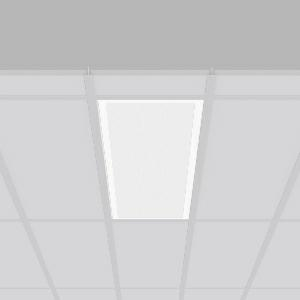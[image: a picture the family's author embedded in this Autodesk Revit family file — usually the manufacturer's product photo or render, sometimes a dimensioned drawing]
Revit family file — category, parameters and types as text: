
# Revit family: sidelite_eco_672375_002_1_1c27
name_source: partatom
category: Lighting Fixtures
units: mm (PartAtom-declared; Revit-internal decimal feet)

## family parameters
Cut with Voids When Loaded = No
Host = Face
Light Source = No
Part Type = Normal
Room Calculation Point = No
Round Connector Dimension = Use Diameter
Shared = No

## types (1)
- SIDELITE ECO (1 x LED Modul 840, 3500 lm, 4000)
    Apparent Load = 29 VA
    CIE Flux Codes = 59 87 97 100 100
    Color Rendering = 80
    Color Temperature = 4000
    Default Elevation = 1800 mm
    Description = Series: SIDELITE ECO
Highly economical recessed luminaire with progressive LED technology. For escape route illumination. Frame made of aluminium, powder-coated. Diffuser plastic microprismatic. Lightguide and diffuser made of non-yellowing plastic (PMMA). Lateral light emission (RZB SIDELITE technology) for homogeneous light distribution. External driver. Self-contained system with automatic self-test. External driver with simple plug-in locking system. Extended connection cable (1.90 m). 
Colour: white
Length: 1245 mm
Width: 308 mm
Cut-out length: 1220 mm
Cut-out width: 285 mm
Recess height: 160 mm
Luminaire: recess height: 40 mm
Weight: 4.7 kg
Operating mode: maintained power mode
Duration time: 8 h
Lamp: LED
Socket: without socket
Colour temperature: 4000K
Colour rendering index (CRI): 80
System power: 29 W
Rated luminous flux: 3500 lm
Luminous flux, emergency: 240 lm
System power, emergency: -
Control gear: Regulated power supply
Protection class: I
Type of protection: IP 40
    Height = 0 mm  [stored 0 ft]
    Lamp = 1 x LED Modul 840
    Lamp Light Flux = 3500 lm
    Lamp count = 1
    Length = 1245 mm
    Lifetime = 50000 h
    Luminous efficacy = 121 lm/W
    Manufacturer = RZB
    ModVariant = No
    Model = 672375.002.1
    Mounting Place = Ceiling
    Mounting Type = Recessed
    Number of Poles = 1
    OnlyDefault = Yes
    Power Factor = 1
    Product Name = SIDELITE ECO
    Product group = Recessed modular luminaires
    ProductGroupID = 406
    Protection Class = Protection class I
    Protection Degree = IP 40
    RLX_Detail_Level = 1
    RLX_Emergency_Light_Flux = 240 lm
    RLX_Emergency_Type = 3
    RLX_Emergency_Type_DB = Yes
    RlxData = <blob elided: 34309 chars, md5=235ae720>
    Socket = socket
    Standby Power = 0 W
    System Light Flux = 3500 lm
    System Power = 29 W
    Type Comments = Product without accessories
    Type Image = 312368.002.jpg
    URL = http://relux.com
    VarID = ---
    Voltage = 230 V
    Voltage Range = 220-240 V
    Weight = 0.00 kg
    Width = 308 mm

note: [stored X ft] marks values corroborated as IEEE doubles in the binary element streams (Revit-internal decimal feet)

## geometry (parser evidence)
native form markers: Blend x4, Sweep x11
no freeform markers — native parametric forms only
